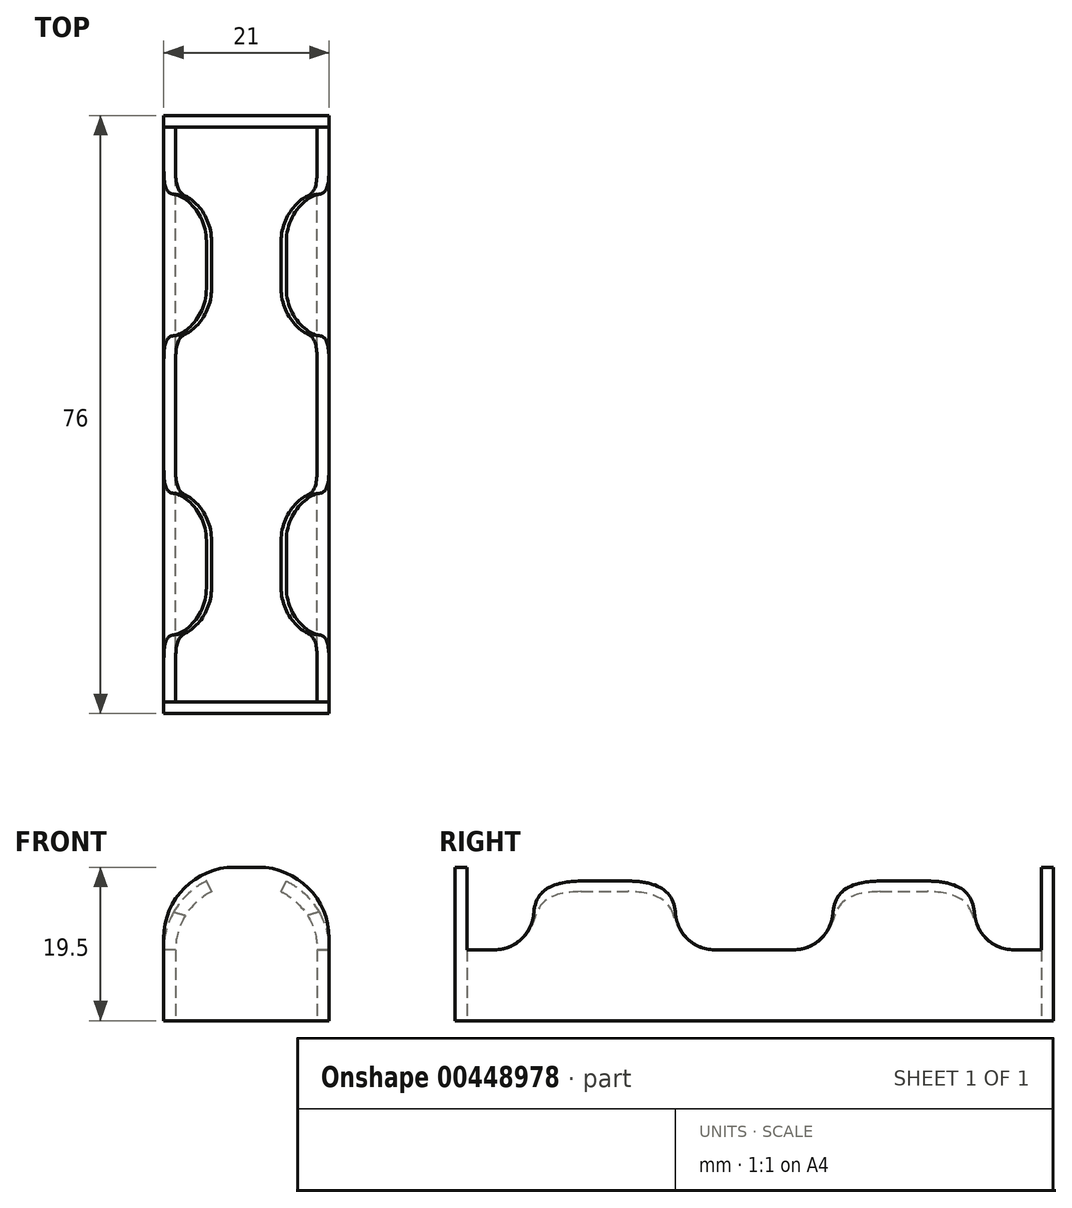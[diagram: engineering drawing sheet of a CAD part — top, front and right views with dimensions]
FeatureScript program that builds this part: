
annotation { "Feature Type Name" : "Feature", "Feature Type Description" : "" }
export const myFeature = defineFeature(function(context is Context, id is Id, definition is map)
    precondition{}
    {
        {
            var Q0;
            Q0=qCreatedBy(makeId("Top.planeOp"),FACE);
            var sketch = newSketch(context, id + "F0", { "sketchPlane" : qUnion([Q0])});
            skLineSegment(sketch, "E0.bottom", {"start": v(0, 0) * mm, "end": v(21, 0) * mm});
            skLineSegment(sketch, "E0.top", {"start": v(0, 76) * mm, "end": v(21, 76) * mm});
            skLineSegment(sketch, "E0.left", {"start": v(0, 0) * mm, "end": v(0, 76) * mm});
            skLineSegment(sketch, "E0.right", {"start": v(21, 0) * mm, "end": v(21, 76) * mm});
            skLineSegment(sketch, "E1.0", {"start": v(1.5, 74.5) * mm, "end": v(19.75, 74.5) * mm});
            skLineSegment(sketch, "E1.1", {"start": v(1.5, 1.5) * mm, "end": v(1.5, 74.5) * mm});
            skLineSegment(sketch, "E1.2", {"start": v(1.5, 1.5) * mm, "end": v(19.75, 1.5) * mm});
            skLineSegment(sketch, "E1.3", {"start": v(19.5, 1.5) * mm, "end": v(19.5, 74.5) * mm});
            skLineSegment(sketch, "E2.trimOffspring", {"start": v(1.25, 74.5) * mm, "end": v(19.5, 74.5) * mm});
            skLineSegment(sketch, "E3.trimOffspring", {"start": v(19.5, 1.5) * mm, "end": v(21.25, 1.5) * mm});
            skLineSegment(sketch, "E4.bottom", {"start": v(0, 66) * mm, "end": v(1.5, 66) * mm});
            skLineSegment(sketch, "E4.top", {"start": v(0, 48) * mm, "end": v(1.5, 48) * mm});
            skLineSegment(sketch, "E4.left", {"start": v(0, 66) * mm, "end": v(0, 48) * mm});
            skLineSegment(sketch, "E4.right", {"start": v(1.5, 66) * mm, "end": v(1.5, 48) * mm});
            skLineSegment(sketch, "E5.bottom", {"start": v(0, 28) * mm, "end": v(1.5, 28) * mm});
            skLineSegment(sketch, "E5.top", {"start": v(0, 10) * mm, "end": v(1.5, 10) * mm});
            skLineSegment(sketch, "E5.left", {"start": v(0, 28) * mm, "end": v(0, 10) * mm});
            skLineSegment(sketch, "E5.right", {"start": v(1.5, 28) * mm, "end": v(1.5, 10) * mm});
            skLineSegment(sketch, "E6.bottom", {"start": v(19.5, 10) * mm, "end": v(21, 10) * mm});
            skLineSegment(sketch, "E6.top", {"start": v(19.5, 28) * mm, "end": v(21, 28) * mm});
            skLineSegment(sketch, "E6.left", {"start": v(19.5, 10) * mm, "end": v(19.5, 28) * mm});
            skLineSegment(sketch, "E6.right", {"start": v(21, 10) * mm, "end": v(21, 28) * mm});
            skLineSegment(sketch, "E7.bottom", {"start": v(19.5, 48) * mm, "end": v(21, 48) * mm});
            skLineSegment(sketch, "E7.top", {"start": v(19.5, 66) * mm, "end": v(21, 66) * mm});
            skLineSegment(sketch, "E7.left", {"start": v(19.5, 48) * mm, "end": v(19.5, 66) * mm});
            skLineSegment(sketch, "E7.right", {"start": v(21, 48) * mm, "end": v(21, 66) * mm});
            skLineSegment(sketch, "E8", {"start": v(19.5, 74.5) * mm, "end": v(21, 74.5) * mm});
            skLineSegment(sketch, "E9", {"start": v(1.5, 74.5) * mm, "end": v(0, 74.5) * mm});
            skLineSegment(sketch, "E10", {"start": v(1.5, 1.5) * mm, "end": v(0, 1.5) * mm});
            skLineSegment(sketch, "E11", {"start": v(19.5, 1.5) * mm, "end": v(21, 1.5) * mm});
            skLineSegment(sketch, "E12", {"start": v(1.25, 74.5) * mm, "end": v(19.75, 74.5) * mm});
            skLineSegment(sketch, "E13", {"start": v(19.75, 1.5) * mm, "end": v(21.25, 1.5) * mm});
            skPoint(sketch, "E14.start.orphan", {"position": v(19.75, 48) * mm});
            skPoint(sketch, "E15.left.start.orphan", {"position": v(19.75, 28) * mm});
            skSolve(sketch);
        }
        {
            var Q0;
            Q0=qCreatedBy(makeId("Front.planeOp"),FACE);
            var sketch = newSketch(context, id + "F1", { "sketchPlane" : qUnion([Q0])});
            skLineSegment(sketch, "E16", {"start": v(0.75, 0) * mm, "end": v(0.75, 9) * mm});
            skArc(sketch, "E17", {"start": v(0.75, 9) * mm, "mid": v(2.1, 13.74) * mm, "end": v(5.75, 17.06) * mm});
            skLineSegment(sketch, "E18", {"start": v(10.5, 0) * mm, "end": v(10.5, 8.81) * mm, "construction": true});
            skLineSegment(sketch, "E19.MirrorCS", {"start": v(20.25, 0) * mm, "end": v(20.25, 9) * mm});
            skArc(sketch, "E20.MirrorCS", {"start": v(20.25, 9) * mm, "mid": v(18.9, 13.74) * mm, "end": v(15.25, 17.06) * mm});
            skSolve(sketch);
        }
        {
            var Q0;
            {var subQ0=sQuery(id+"F0.wireOp",EDGE,"E2.trimOffspring");Q0=makeQuery(id+"F0.imprint","IMPRINT",FACE,{"disambiguationData":[TD([[makeQuery(id+"F0.imprint","IMPRINT",EDGE,{"derivedFrom":subQ0}),-1.0]])]});}
            var Q1;
            {var subQ0=sQuery(id+"F0.wireOp",EDGE,"E4.top");Q1=makeQuery(id+"F0.imprint","IMPRINT",FACE,{"disambiguationData":[TD([[makeQuery(id+"F0.imprint","IMPRINT",EDGE,{"derivedFrom":subQ0}),-1.0]])]});}
            var Q2;
            {var subQ0=sQuery(id+"F0.wireOp",EDGE,"E4.bottom");Q2=makeQuery(id+"F0.imprint","IMPRINT",FACE,{"disambiguationData":[TD([[makeQuery(id+"F0.imprint","IMPRINT",EDGE,{"derivedFrom":subQ0}),1.0]])]});}
            var Q3;
            {var subQ0=sQuery(id+"F0.wireOp",EDGE,"E6.bottom");Q3=makeQuery(id+"F0.imprint","IMPRINT",FACE,{"disambiguationData":[TD([[makeQuery(id+"F0.imprint","IMPRINT",EDGE,{"derivedFrom":subQ0}),-1.0]])]});}
            var Q4;
            {var subQ0=sQuery(id+"F0.wireOp",EDGE,"E6.top");Q4=makeQuery(id+"F0.imprint","IMPRINT",FACE,{"disambiguationData":[TD([[makeQuery(id+"F0.imprint","IMPRINT",EDGE,{"derivedFrom":subQ0}),1.0]])]});}
            var Q5;
            {var subQ0=sQuery(id+"F0.wireOp",EDGE,"E7.top");Q5=makeQuery(id+"F0.imprint","IMPRINT",FACE,{"disambiguationData":[TD([[makeQuery(id+"F0.imprint","IMPRINT",EDGE,{"derivedFrom":subQ0}),1.0]])]});}
            var Q6;
            Q6=makeQuery(id+"F0.imprint","IMPRINT",FACE,{"disambiguationData":[TD([[makeQuery(id+"F0.imprint","IMPRINT",EDGE,{"derivedFrom":sQuery(id+"F0.wireOp",EDGE,"E4.bottom")}),-1.0]])]});
            var Q7;
            Q7=makeQuery(id+"F0.imprint","IMPRINT",FACE,{"disambiguationData":[TD([[makeQuery(id+"F0.imprint","IMPRINT",EDGE,{"derivedFrom":sQuery(id+"F0.wireOp",EDGE,"E6.bottom")}),1.0]])]});
            var Q8;
            Q8=makeQuery(id+"F0.imprint","IMPRINT",FACE,{"disambiguationData":[TD([[makeQuery(id+"F0.imprint","IMPRINT",EDGE,{"derivedFrom":sQuery(id+"F0.wireOp",EDGE,"E7.bottom")}),1.0]])]});
            var Q9;
            {var subQ0=sQuery(id+"F0.wireOp",EDGE,"E54Q2sP0-sC4c-n17p-ldyP-ap2FQRhICNUg");Q9=makeQuery(id+"F0.imprint","IMPRINT",FACE,{"disambiguationData":[TD([[makeQuery(id+"F0.imprint","IMPRINT",EDGE,{"derivedFrom":subQ0}),1.0]])]});}
            var Q10;
            {var subQ2=sQuery(id+"F0.wireOp",EDGE,"E0.top");Q10=makeQuery(id+"F0.imprint","IMPRINT",FACE,{"disambiguationData":[TD([[makeQuery(id+"F0.imprint","IMPRINT",EDGE,{"derivedFrom":subQ2}),-1.0]])]});}
            var Q11;
            {var subQ0=sQuery(id+"F0.wireOp",EDGE,"E5.top");Q11=makeQuery(id+"F0.imprint","IMPRINT",FACE,{"disambiguationData":[TD([[makeQuery(id+"F0.imprint","IMPRINT",EDGE,{"derivedFrom":subQ0}),-1.0]])]});}
            var Q12;
            {var subQ1=sQuery(id+"F0.wireOp",EDGE,"E0.bottom");Q12=makeQuery(id+"F0.imprint","IMPRINT",FACE,{"disambiguationData":[TD([[makeQuery(id+"F0.imprint","IMPRINT",EDGE,{"derivedFrom":subQ1}),1.0]])]});}
            var Q13;
            {var subQ1=sQuery(id+"F0.wireOp",EDGE,"E1.0");Q13=makeQuery(id+"F0.imprint","IMPRINT",FACE,{"disambiguationData":[TD([[makeQuery(id+"F0.imprint","IMPRINT",EDGE,{"derivedFrom":subQ1}),-1.0]])]});}
            var Q14;
            Q14=makeQuery(id+"F0.imprint","IMPRINT",FACE,{"disambiguationData":[TD([[makeQuery(id+"F0.imprint","IMPRINT",EDGE,{"derivedFrom":sQuery(id+"F0.wireOp",EDGE,"E5.bottom")}),-1.0]])]});
            extrude(context, id + "F2", {"entities" : qUnion([Q0, Q1, Q2, Q3, Q4, Q5, Q6, Q7, Q8, Q9, Q10, Q11, Q12, Q13, Q14]), "depth" : 1.5 * mm});
        }
        {
            var Q0;
            {var subQ2=sQuery(id+"F0.wireOp",EDGE,"E0.top");Q0=makeQuery(id+"F0.imprint","IMPRINT",FACE,{"disambiguationData":[TD([[makeQuery(id+"F0.imprint","IMPRINT",EDGE,{"derivedFrom":subQ2}),-1.0]])]});}
            var Q1;
            {var subQ1=sQuery(id+"F0.wireOp",EDGE,"E0.bottom");Q1=makeQuery(id+"F0.imprint","IMPRINT",FACE,{"disambiguationData":[TD([[makeQuery(id+"F0.imprint","IMPRINT",EDGE,{"derivedFrom":subQ1}),1.0]])]});}
            extrude(context, id + "F3", {"entities" : qUnion([Q0, Q1]), "operationType" : NewBodyOperationType.ADD, "depth" : 19.5 * mm});
        }
        {
            var Q0;
            {var subQ0=sQuery(id+"F0.wireOp",EDGE,"E4.top");Q0=makeQuery(id+"F0.imprint","IMPRINT",FACE,{"disambiguationData":[TD([[makeQuery(id+"F0.imprint","IMPRINT",EDGE,{"derivedFrom":subQ0}),-1.0]])]});}
            var Q1;
            Q1=makeQuery(id+"F0.imprint","IMPRINT",FACE,{"disambiguationData":[TD([[makeQuery(id+"F0.imprint","IMPRINT",EDGE,{"derivedFrom":sQuery(id+"F0.wireOp",EDGE,"E5.bottom")}),-1.0]])]});
            var Q2;
            {var subQ0=sQuery(id+"F0.wireOp",EDGE,"E5.top");Q2=makeQuery(id+"F0.imprint","IMPRINT",FACE,{"disambiguationData":[TD([[makeQuery(id+"F0.imprint","IMPRINT",EDGE,{"derivedFrom":subQ0}),-1.0]])]});}
            var Q3;
            Q3=makeQuery(id+"F0.imprint","IMPRINT",FACE,{"disambiguationData":[TD([[makeQuery(id+"F0.imprint","IMPRINT",EDGE,{"derivedFrom":sQuery(id+"F0.wireOp",EDGE,"E4.bottom")}),-1.0]])]});
            var Q4;
            {var subQ0=sQuery(id+"F0.wireOp",EDGE,"E4.bottom");Q4=makeQuery(id+"F0.imprint","IMPRINT",FACE,{"disambiguationData":[TD([[makeQuery(id+"F0.imprint","IMPRINT",EDGE,{"derivedFrom":subQ0}),1.0]])]});}
            var Q5;
            {var subQ0=sQuery(id+"F0.wireOp",EDGE,"E7.top");Q5=makeQuery(id+"F0.imprint","IMPRINT",FACE,{"disambiguationData":[TD([[makeQuery(id+"F0.imprint","IMPRINT",EDGE,{"derivedFrom":subQ0}),1.0]])]});}
            var Q6;
            Q6=makeQuery(id+"F0.imprint","IMPRINT",FACE,{"disambiguationData":[TD([[makeQuery(id+"F0.imprint","IMPRINT",EDGE,{"derivedFrom":sQuery(id+"F0.wireOp",EDGE,"E7.bottom")}),1.0]])]});
            var Q7;
            {var subQ0=sQuery(id+"F0.wireOp",EDGE,"E6.top");Q7=makeQuery(id+"F0.imprint","IMPRINT",FACE,{"disambiguationData":[TD([[makeQuery(id+"F0.imprint","IMPRINT",EDGE,{"derivedFrom":subQ0}),1.0]])]});}
            var Q8;
            Q8=makeQuery(id+"F0.imprint","IMPRINT",FACE,{"disambiguationData":[TD([[makeQuery(id+"F0.imprint","IMPRINT",EDGE,{"derivedFrom":sQuery(id+"F0.wireOp",EDGE,"E6.bottom")}),1.0]])]});
            var Q9;
            {var subQ0=sQuery(id+"F0.wireOp",EDGE,"E6.bottom");Q9=makeQuery(id+"F0.imprint","IMPRINT",FACE,{"disambiguationData":[TD([[makeQuery(id+"F0.imprint","IMPRINT",EDGE,{"derivedFrom":subQ0}),-1.0]])]});}
            extrude(context, id + "F4", {"entities" : qUnion([Q0, Q1, Q2, Q3, Q4, Q5, Q6, Q7, Q8, Q9]), "operationType" : NewBodyOperationType.ADD, "depth" : 9 * mm});
        }
        {
            var Q0;
            Q0=makeQuery(id+"F0.imprint","IMPRINT",FACE,{"disambiguationData":[TD([[makeQuery(id+"F0.imprint","IMPRINT",EDGE,{"derivedFrom":sQuery(id+"F0.wireOp",EDGE,"E5.bottom")}),-1.0]])]});
            var Q1;
            Q1=makeQuery(id+"F0.imprint","IMPRINT",FACE,{"disambiguationData":[TD([[makeQuery(id+"F0.imprint","IMPRINT",EDGE,{"derivedFrom":sQuery(id+"F0.wireOp",EDGE,"E4.bottom")}),-1.0]])]});
            var Q2;
            Q2=sQuery(id+"F1.wireOp",EDGE,"E16");
            var Q3;
            Q3=sQuery(id+"F1.wireOp",EDGE,"E17");
            sweep(context, id + "F5", {"operationType" : NewBodyOperationType.ADD, "profiles" : qUnion([Q0, Q1]), "path" : qUnion([Q2, Q3])});
        }
        {
            var Q0;
            Q0=makeQuery(id+"F0.imprint","IMPRINT",FACE,{"disambiguationData":[TD([[makeQuery(id+"F0.imprint","IMPRINT",EDGE,{"derivedFrom":sQuery(id+"F0.wireOp",EDGE,"E7.bottom")}),1.0]])]});
            var Q1;
            Q1=makeQuery(id+"F0.imprint","IMPRINT",FACE,{"disambiguationData":[TD([[makeQuery(id+"F0.imprint","IMPRINT",EDGE,{"derivedFrom":sQuery(id+"F0.wireOp",EDGE,"E6.bottom")}),1.0]])]});
            var Q2;
            Q2=sQuery(id+"F1.wireOp",EDGE,"E20.MirrorCS");
            var Q3;
            Q3=sQuery(id+"F1.wireOp",EDGE,"E19.MirrorCS");
            sweep(context, id + "F6", {"operationType" : NewBodyOperationType.ADD, "profiles" : qUnion([Q0, Q1]), "path" : qUnion([Q2, Q3])});
        }
        {
            var Q0;
            {var subQ0=sQuery(id+"F0.wireOp",EDGE,"E0.left");Q0=makeQuery(id+"F3.opExtrude","CAP_EDGE",EDGE,{"disambiguationData":[OSD([subQ0]),TDD([makeQuery(id+"F0.imprint","IMPRINT",EDGE,{"disambiguationData":[TD([[makeQuery(id+"F0.imprint","INTERSECT",VERTEX,{"derivedFrom":[sQuery(id+"F0.wireOp",EDGE,"E0.bottom"),subQ0]}),-1.0]])],"derivedFrom":subQ0})])],"isStart":false});}
            var Q1;
            {var subQ0=sQuery(id+"F0.wireOp",EDGE,"E0.right");Q1=makeQuery(id+"F3.opExtrude","CAP_EDGE",EDGE,{"disambiguationData":[OSD([subQ0]),TDD([makeQuery(id+"F0.imprint","IMPRINT",EDGE,{"disambiguationData":[TD([[makeQuery(id+"F0.imprint","INTERSECT",VERTEX,{"derivedFrom":[sQuery(id+"F0.wireOp",EDGE,"E0.bottom"),subQ0]}),-1.0]])],"derivedFrom":subQ0})])],"isStart":false});}
            var Q2;
            {var subQ0=sQuery(id+"F0.wireOp",EDGE,"E0.right");Q2=makeQuery(id+"F3.opExtrude","CAP_EDGE",EDGE,{"disambiguationData":[OSD([subQ0]),TDD([makeQuery(id+"F0.imprint","IMPRINT",EDGE,{"disambiguationData":[TD([[makeQuery(id+"F0.imprint","INTERSECT",VERTEX,{"derivedFrom":[sQuery(id+"F0.wireOp",EDGE,"E0.top"),subQ0]}),1.0]])],"derivedFrom":subQ0})])],"isStart":false});}
            var Q3;
            {var subQ0=sQuery(id+"F0.wireOp",EDGE,"E0.left");Q3=makeQuery(id+"F3.opExtrude","CAP_EDGE",EDGE,{"disambiguationData":[OSD([subQ0]),TDD([makeQuery(id+"F0.imprint","IMPRINT",EDGE,{"disambiguationData":[TD([[makeQuery(id+"F0.imprint","INTERSECT",VERTEX,{"derivedFrom":[sQuery(id+"F0.wireOp",EDGE,"E0.top"),subQ0]}),1.0]])],"derivedFrom":subQ0})])],"isStart":false});}
            fillet(context, id + "F7", {"entities" : qUnion([Q0, Q1, Q2, Q3]), "radius" : 9 * mm, "tangentPropagation" : true, "allowEdgeOverflow" : false});
        }
        {
            var Q0;
            Q0=makeQuery(id+"F6.opSweep","CAP_EDGE",EDGE,{"disambiguationData":[OSD([sQuery(id+"F0.wireOp",EDGE,"E6.top"),sQuery(id+"F1.wireOp",VERTEX,"E20.MirrorCS.end")])],"isStart":false});
            var Q1;
            Q1=makeQuery(id+"F5.opSweep","CAP_EDGE",EDGE,{"disambiguationData":[OSD([sQuery(id+"F0.wireOp",EDGE,"E5.bottom"),sQuery(id+"F1.wireOp",VERTEX,"E17.end")])],"isStart":false});
            var Q2;
            Q2=makeQuery(id+"F5.opSweep","CAP_EDGE",EDGE,{"disambiguationData":[OSD([sQuery(id+"F0.wireOp",EDGE,"E5.top"),sQuery(id+"F1.wireOp",VERTEX,"E17.end")])],"isStart":false});
            var Q3;
            Q3=makeQuery(id+"F5.opSweep","CAP_EDGE",EDGE,{"disambiguationData":[OSD([sQuery(id+"F0.wireOp",EDGE,"E4.top"),sQuery(id+"F1.wireOp",VERTEX,"E17.end")])],"isStart":false});
            var Q4;
            Q4=makeQuery(id+"F5.opSweep","CAP_EDGE",EDGE,{"disambiguationData":[OSD([sQuery(id+"F0.wireOp",EDGE,"E4.bottom"),sQuery(id+"F1.wireOp",VERTEX,"E17.end")])],"isStart":false});
            var Q5;
            Q5=makeQuery(id+"F6.opSweep","CAP_EDGE",EDGE,{"disambiguationData":[OSD([sQuery(id+"F0.wireOp",EDGE,"E7.top"),sQuery(id+"F1.wireOp",VERTEX,"E20.MirrorCS.end")])],"isStart":false});
            var Q6;
            Q6=makeQuery(id+"F6.opSweep","CAP_EDGE",EDGE,{"disambiguationData":[OSD([sQuery(id+"F0.wireOp",EDGE,"E7.bottom"),sQuery(id+"F1.wireOp",VERTEX,"E20.MirrorCS.end")])],"isStart":false});
            var Q7;
            Q7=makeQuery(id+"F6.opSweep","CAP_EDGE",EDGE,{"disambiguationData":[OSD([sQuery(id+"F0.wireOp",EDGE,"E6.bottom"),sQuery(id+"F1.wireOp",VERTEX,"E20.MirrorCS.end")])],"isStart":false});
            fillet(context, id + "F8", {"entities" : qUnion([Q0, Q1, Q2, Q3, Q4, Q5, Q6, Q7]), "radius" : 6 * mm, "tangentPropagation" : true, "allowEdgeOverflow" : false});
        }
        {
            var Q0;
            Q0=makeQuery(id+"F6.boolean.opBoolean","INTERSECT",EDGE,{"derivedFrom":[makeQuery(id+"F4.opExtrude","CAP_FACE",FACE,{"disambiguationData":[OSD([sQuery(id+"F0.wireOp",EDGE,"E0.right"),sQuery(id+"F0.wireOp",EDGE,"E1.3"),sQuery(id+"F0.wireOp",EDGE,"E6.left"),sQuery(id+"F0.wireOp",EDGE,"E6.right"),sQuery(id+"F0.wireOp",EDGE,"E7.left"),sQuery(id+"F0.wireOp",EDGE,"E7.right"),sQuery(id+"F0.wireOp",EDGE,"E8"),sQuery(id+"F0.wireOp",EDGE,"E11")])],"isStart":false}),makeQuery(id+"F6.opSweep","SWEPT_FACE",FACE,{"disambiguationData":[OSD([sQuery(id+"F0.wireOp",EDGE,"E6.bottom"),sQuery(id+"F1.wireOp",EDGE,"E19.MirrorCS")])]})]});
            var Q1;
            Q1=makeQuery(id+"F6.boolean.opBoolean","INTERSECT",EDGE,{"derivedFrom":[makeQuery(id+"F4.opExtrude","CAP_FACE",FACE,{"disambiguationData":[OSD([sQuery(id+"F0.wireOp",EDGE,"E0.right"),sQuery(id+"F0.wireOp",EDGE,"E1.3"),sQuery(id+"F0.wireOp",EDGE,"E6.left"),sQuery(id+"F0.wireOp",EDGE,"E6.right"),sQuery(id+"F0.wireOp",EDGE,"E7.left"),sQuery(id+"F0.wireOp",EDGE,"E7.right"),sQuery(id+"F0.wireOp",EDGE,"E8"),sQuery(id+"F0.wireOp",EDGE,"E11")])],"isStart":false}),makeQuery(id+"F6.opSweep","SWEPT_FACE",FACE,{"disambiguationData":[OSD([sQuery(id+"F0.wireOp",EDGE,"E7.bottom"),sQuery(id+"F1.wireOp",EDGE,"E19.MirrorCS")])]})]});
            var Q2;
            Q2=makeQuery(id+"F5.boolean.opBoolean","INTERSECT",EDGE,{"derivedFrom":[makeQuery(id+"F4.opExtrude","CAP_FACE",FACE,{"disambiguationData":[OSD([sQuery(id+"F0.wireOp",EDGE,"E0.left"),sQuery(id+"F0.wireOp",EDGE,"E1.1"),sQuery(id+"F0.wireOp",EDGE,"E4.left"),sQuery(id+"F0.wireOp",EDGE,"E4.right"),sQuery(id+"F0.wireOp",EDGE,"E5.left"),sQuery(id+"F0.wireOp",EDGE,"E5.right"),sQuery(id+"F0.wireOp",EDGE,"E9"),sQuery(id+"F0.wireOp",EDGE,"E10")])],"isStart":false}),makeQuery(id+"F5.opSweep","SWEPT_FACE",FACE,{"disambiguationData":[OSD([sQuery(id+"F0.wireOp",EDGE,"E4.top"),sQuery(id+"F1.wireOp",EDGE,"E16")])]})]});
            var Q3;
            Q3=makeQuery(id+"F6.boolean.opBoolean","INTERSECT",EDGE,{"derivedFrom":[makeQuery(id+"F4.opExtrude","CAP_FACE",FACE,{"disambiguationData":[OSD([sQuery(id+"F0.wireOp",EDGE,"E0.right"),sQuery(id+"F0.wireOp",EDGE,"E1.3"),sQuery(id+"F0.wireOp",EDGE,"E6.left"),sQuery(id+"F0.wireOp",EDGE,"E6.right"),sQuery(id+"F0.wireOp",EDGE,"E7.left"),sQuery(id+"F0.wireOp",EDGE,"E7.right"),sQuery(id+"F0.wireOp",EDGE,"E8"),sQuery(id+"F0.wireOp",EDGE,"E11")])],"isStart":false}),makeQuery(id+"F6.opSweep","SWEPT_FACE",FACE,{"disambiguationData":[OSD([sQuery(id+"F0.wireOp",EDGE,"E6.top"),sQuery(id+"F1.wireOp",EDGE,"E19.MirrorCS")])]})]});
            var Q4;
            Q4=makeQuery(id+"F6.boolean.opBoolean","INTERSECT",EDGE,{"derivedFrom":[makeQuery(id+"F4.opExtrude","CAP_FACE",FACE,{"disambiguationData":[OSD([sQuery(id+"F0.wireOp",EDGE,"E0.right"),sQuery(id+"F0.wireOp",EDGE,"E1.3"),sQuery(id+"F0.wireOp",EDGE,"E6.left"),sQuery(id+"F0.wireOp",EDGE,"E6.right"),sQuery(id+"F0.wireOp",EDGE,"E7.left"),sQuery(id+"F0.wireOp",EDGE,"E7.right"),sQuery(id+"F0.wireOp",EDGE,"E8"),sQuery(id+"F0.wireOp",EDGE,"E11")])],"isStart":false}),makeQuery(id+"F6.opSweep","SWEPT_FACE",FACE,{"disambiguationData":[OSD([sQuery(id+"F0.wireOp",EDGE,"E7.top"),sQuery(id+"F1.wireOp",EDGE,"E19.MirrorCS")])]})]});
            var Q5;
            Q5=makeQuery(id+"F5.boolean.opBoolean","INTERSECT",EDGE,{"derivedFrom":[makeQuery(id+"F4.opExtrude","CAP_FACE",FACE,{"disambiguationData":[OSD([sQuery(id+"F0.wireOp",EDGE,"E0.left"),sQuery(id+"F0.wireOp",EDGE,"E1.1"),sQuery(id+"F0.wireOp",EDGE,"E4.left"),sQuery(id+"F0.wireOp",EDGE,"E4.right"),sQuery(id+"F0.wireOp",EDGE,"E5.left"),sQuery(id+"F0.wireOp",EDGE,"E5.right"),sQuery(id+"F0.wireOp",EDGE,"E9"),sQuery(id+"F0.wireOp",EDGE,"E10")])],"isStart":false}),makeQuery(id+"F5.opSweep","SWEPT_FACE",FACE,{"disambiguationData":[OSD([sQuery(id+"F0.wireOp",EDGE,"E5.bottom"),sQuery(id+"F1.wireOp",EDGE,"E16")])]})]});
            var Q6;
            Q6=makeQuery(id+"F5.boolean.opBoolean","INTERSECT",EDGE,{"derivedFrom":[makeQuery(id+"F4.opExtrude","CAP_FACE",FACE,{"disambiguationData":[OSD([sQuery(id+"F0.wireOp",EDGE,"E0.left"),sQuery(id+"F0.wireOp",EDGE,"E1.1"),sQuery(id+"F0.wireOp",EDGE,"E4.left"),sQuery(id+"F0.wireOp",EDGE,"E4.right"),sQuery(id+"F0.wireOp",EDGE,"E5.left"),sQuery(id+"F0.wireOp",EDGE,"E5.right"),sQuery(id+"F0.wireOp",EDGE,"E9"),sQuery(id+"F0.wireOp",EDGE,"E10")])],"isStart":false}),makeQuery(id+"F5.opSweep","SWEPT_FACE",FACE,{"disambiguationData":[OSD([sQuery(id+"F0.wireOp",EDGE,"E4.bottom"),sQuery(id+"F1.wireOp",EDGE,"E16")])]})]});
            var Q7;
            Q7=makeQuery(id+"F5.boolean.opBoolean","INTERSECT",EDGE,{"derivedFrom":[makeQuery(id+"F4.opExtrude","CAP_FACE",FACE,{"disambiguationData":[OSD([sQuery(id+"F0.wireOp",EDGE,"E0.left"),sQuery(id+"F0.wireOp",EDGE,"E1.1"),sQuery(id+"F0.wireOp",EDGE,"E4.left"),sQuery(id+"F0.wireOp",EDGE,"E4.right"),sQuery(id+"F0.wireOp",EDGE,"E5.left"),sQuery(id+"F0.wireOp",EDGE,"E5.right"),sQuery(id+"F0.wireOp",EDGE,"E9"),sQuery(id+"F0.wireOp",EDGE,"E10")])],"isStart":false}),makeQuery(id+"F5.opSweep","SWEPT_FACE",FACE,{"disambiguationData":[OSD([sQuery(id+"F0.wireOp",EDGE,"E5.top"),sQuery(id+"F1.wireOp",EDGE,"E16")])]})]});
            fillet(context, id + "F9", {"entities" : qUnion([Q0, Q1, Q2, Q3, Q4, Q5, Q6, Q7]), "radius" : 5 * mm, "tangentPropagation" : true, "allowEdgeOverflow" : false});
        }
        {
            var Q0;
            {var subQ2=sQuery(id+"F0.wireOp",EDGE,"E1.2");Q0=makeQuery(id+"F0.imprint","IMPRINT",FACE,{"disambiguationData":[TD([[makeQuery(id+"F0.imprint","IMPRINT",EDGE,{"derivedFrom":subQ2}),1.0]])]});}
            extrude(context, id + "F10", {"entities" : qUnion([Q0]), "operationType" : NewBodyOperationType.ADD, "depth" : 1.5 * mm});
        }
    });
